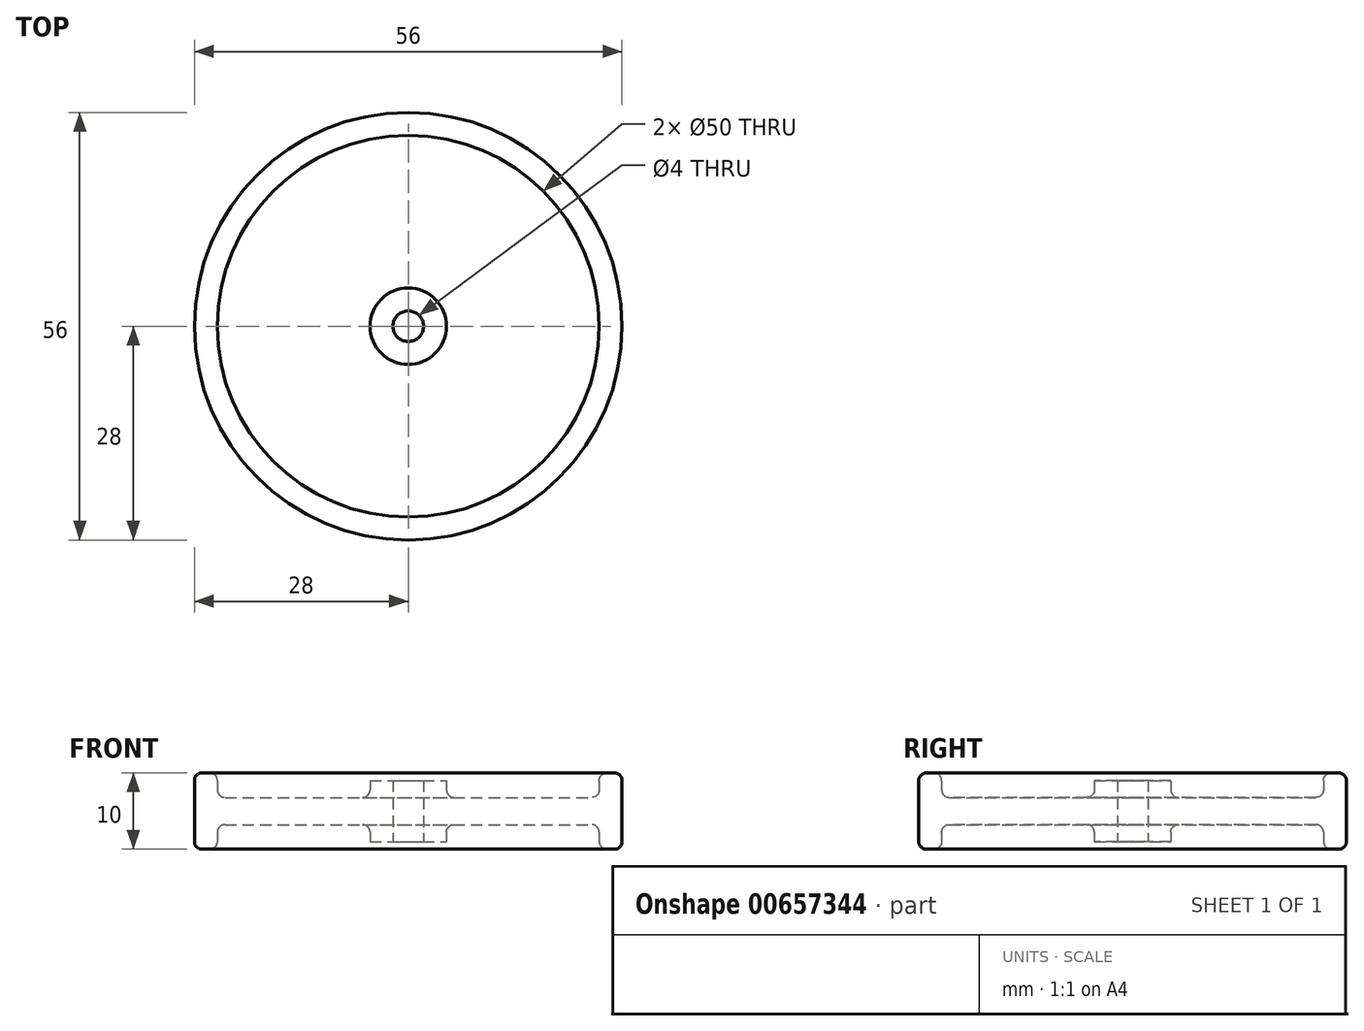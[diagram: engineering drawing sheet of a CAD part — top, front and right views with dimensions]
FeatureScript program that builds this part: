
annotation { "Feature Type Name" : "Feature", "Feature Type Description" : "" }
export const myFeature = defineFeature(function(context is Context, id is Id, definition is map)
    precondition{}
    {
        {
            var Q0;
            Q0=qCreatedBy(makeId("Front.planeOp"),FACE);
            var sketch = newSketch(context, id + "F0", { "sketchPlane" : qUnion([Q0])});
            skLineSegment(sketch, "E0.bottom", {"start": v(2, -4) * mm, "end": v(5, -4) * mm});
            skLineSegment(sketch, "E0.top", {"start": v(2, 4) * mm, "end": v(5, 4) * mm});
            skLineSegment(sketch, "E0.left", {"start": v(2, -4) * mm, "end": v(2, 4) * mm});
            skLineSegment(sketch, "E0.right", {"start": v(5, -4) * mm, "end": v(5, -2.78) * mm});
            skLineSegment(sketch, "E1.bottom", {"start": v(6, 1.78) * mm, "end": v(24, 1.78) * mm});
            skLineSegment(sketch, "E1.top", {"start": v(6, -1.78) * mm, "end": v(24, -1.78) * mm});
            skLineSegment(sketch, "E2.bottom", {"start": v(26, 5) * mm, "end": v(27, 5) * mm});
            skLineSegment(sketch, "E2.top", {"start": v(26, -5) * mm, "end": v(27, -5) * mm});
            skLineSegment(sketch, "E2.left", {"start": v(25, 4) * mm, "end": v(25, 2.78) * mm});
            skLineSegment(sketch, "E2.right", {"start": v(28, 4) * mm, "end": v(28, -4) * mm});
            skLineSegment(sketch, "E3.trimOffspring", {"start": v(5, 2.78) * mm, "end": v(5, 4) * mm});
            skLineSegment(sketch, "E4.trimOffspring", {"start": v(25, -2.78) * mm, "end": v(25, -4) * mm});
            skLineSegment(sketch, "E5", {"start": v(2, 0) * mm, "end": v(28, 0) * mm, "construction": true});
            skPoint(sketch, "E6.visualSharp", {"position": v(25, 5) * mm});
            skArc(sketch, "E6.filletArc", {"start": v(26, 5) * mm, "mid": v(25.3, 4.7) * mm, "end": v(25, 4) * mm});
            skPoint(sketch, "E7.visualSharp", {"position": v(28, 5) * mm});
            skArc(sketch, "E7.filletArc", {"start": v(28, 4) * mm, "mid": v(27.7, 4.7) * mm, "end": v(27, 5) * mm});
            skPoint(sketch, "E8.visualSharp", {"position": v(28, -5) * mm});
            skArc(sketch, "E8.filletArc", {"start": v(27, -5) * mm, "mid": v(27.7, -4.7) * mm, "end": v(28, -4) * mm});
            skPoint(sketch, "E9.visualSharp", {"position": v(25, -5) * mm});
            skArc(sketch, "E9.filletArc", {"start": v(25, -4) * mm, "mid": v(25.3, -4.7) * mm, "end": v(26, -5) * mm});
            skPoint(sketch, "E10.visualSharp", {"position": v(5, 1.78) * mm});
            skArc(sketch, "E10.filletArc", {"start": v(5, 2.78) * mm, "mid": v(5.3, 2.08) * mm, "end": v(6, 1.78) * mm});
            skPoint(sketch, "E11.visualSharp", {"position": v(5, -1.78) * mm});
            skArc(sketch, "E11.filletArc", {"start": v(6, -1.78) * mm, "mid": v(5.3, -2.08) * mm, "end": v(5, -2.78) * mm});
            skPoint(sketch, "E12.visualSharp", {"position": v(25, 1.78) * mm});
            skArc(sketch, "E12.filletArc", {"start": v(24, 1.78) * mm, "mid": v(24.7, 2.08) * mm, "end": v(25, 2.78) * mm});
            skPoint(sketch, "E13.visualSharp", {"position": v(25, -1.78) * mm});
            skArc(sketch, "E13.filletArc", {"start": v(25, -2.78) * mm, "mid": v(24.7, -2.08) * mm, "end": v(24, -1.78) * mm});
            skLineSegment(sketch, "E14", {"start": v(0, 0) * mm, "end": v(0, 23.79) * mm, "construction": true});
            skSolve(sketch);
        }
        {
            var Q0;
            Q0=makeQuery(id+"F0.imprint","IMPRINT",FACE,{"disambiguationData":[TD([[makeQuery(id+"F0.imprint","IMPRINT",EDGE,{"derivedFrom":sQuery(id+"F0.wireOp",EDGE,"E0.bottom")}),1.0]])]});
            var Q1;
            Q1=sQuery(id+"F0.wireOp",EDGE,"E14");
            revolve(context, id + "F1", {"entities" : qUnion([Q0]), "axis" : qUnion([Q1]), "revolveType" : RevolveType.FULL});
        }
    });
